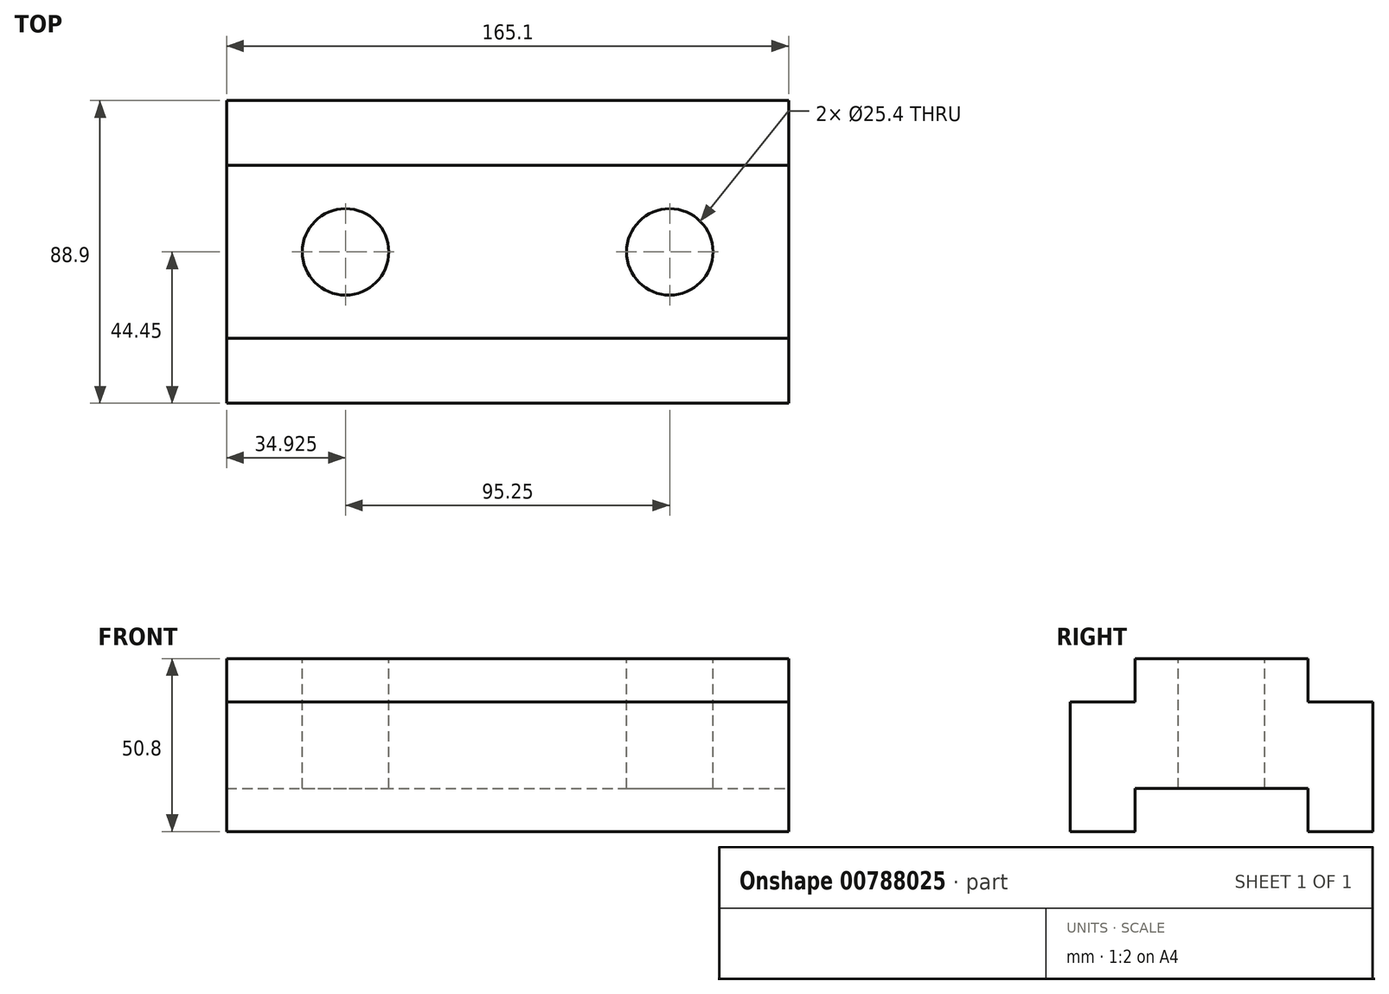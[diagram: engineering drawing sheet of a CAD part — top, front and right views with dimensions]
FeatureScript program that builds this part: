
annotation { "Feature Type Name" : "Feature", "Feature Type Description" : "" }
export const myFeature = defineFeature(function(context is Context, id is Id, definition is map)
    precondition{}
    {
        {
            var Q0;
            Q0=qCreatedBy(makeId("Right.planeOp"),FACE);
            var sketch = newSketch(context, id + "F0", { "sketchPlane" : qUnion([Q0])});
            skLineSegment(sketch, "E0", {"start": v(0, 0) * mm, "end": v(19.05, 0) * mm});
            skLineSegment(sketch, "E1", {"start": v(19.05, 0) * mm, "end": v(19.05, 12.7) * mm});
            skLineSegment(sketch, "E2", {"start": v(19.05, 12.7) * mm, "end": v(69.85, 12.7) * mm});
            skLineSegment(sketch, "E3", {"start": v(69.85, 12.7) * mm, "end": v(69.85, 0) * mm});
            skLineSegment(sketch, "E4", {"start": v(69.85, 0) * mm, "end": v(88.9, 0) * mm});
            skLineSegment(sketch, "E5", {"start": v(88.9, 0) * mm, "end": v(88.9, 38.1) * mm});
            skLineSegment(sketch, "E6", {"start": v(88.9, 38.1) * mm, "end": v(69.85, 38.1) * mm});
            skLineSegment(sketch, "E7", {"start": v(69.85, 38.1) * mm, "end": v(69.85, 50.8) * mm});
            skLineSegment(sketch, "E8", {"start": v(69.85, 50.8) * mm, "end": v(19.05, 50.8) * mm});
            skLineSegment(sketch, "E9", {"start": v(19.05, 50.8) * mm, "end": v(19.05, 38.1) * mm});
            skLineSegment(sketch, "E10", {"start": v(19.05, 38.1) * mm, "end": v(0, 38.1) * mm});
            skLineSegment(sketch, "E11", {"start": v(0, 38.1) * mm, "end": v(0, 0) * mm});
            skSolve(sketch);
        }
        {
            var Q0;
            Q0 = qSketchRegion(id + "F0", true);
            extrude(context, id + "F1", {"entities" : qUnion([Q0]), "oppositeDirection" : true, "depth" : 165.1 * mm, "offsetDistance" : 25.4 * mm});
        }
        {
            var Q0;
            Q0=makeQuery(id+"F1.opExtrude","SWEPT_FACE",FACE,{"disambiguationData":[OSD([sQuery(id+"F0.wireOp",EDGE,"E8")])]});
            var sketch = newSketch(context, id + "F2", { "sketchPlane" : qUnion([Q0])});
            skLineSegment(sketch, "E12", {"start": v(-165.1, 44.45) * mm, "end": v(-130.18, 44.45) * mm, "construction": true});
            skLineSegment(sketch, "E13", {"start": v(-130.18, 44.45) * mm, "end": v(-34.92, 44.45) * mm, "construction": true});
            skCircle(sketch, "E14", {"center": v(-130.18, 44.45) * mm, "radius": 12.7 * mm});
            skCircle(sketch, "E15", {"center": v(-34.92, 44.45) * mm, "radius": 12.7 * mm});
            skSolve(sketch);
        }
        {
            var Q0;
            Q0 = qSketchRegion(id + "F2", true);
            extrude(context, id + "F3", {"entities" : qUnion([Q0]), "operationType" : NewBodyOperationType.REMOVE, "endBound" : BoundingType.UP_TO_NEXT, "oppositeDirection" : true, "depth" : 25.4 * mm, "offsetDistance" : 25.4 * mm});
        }
    });
